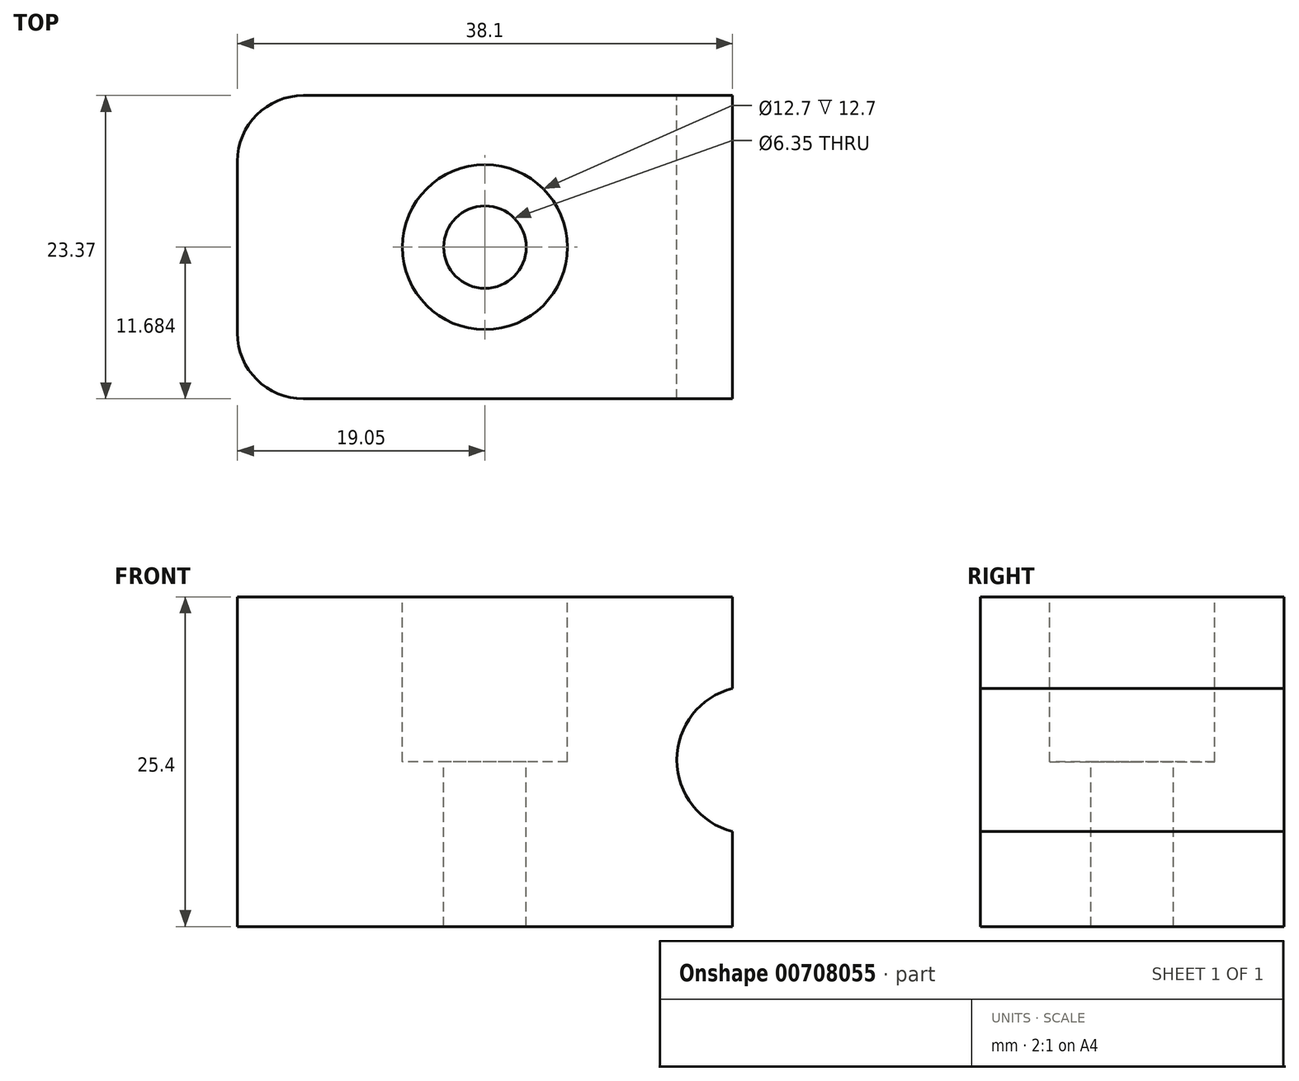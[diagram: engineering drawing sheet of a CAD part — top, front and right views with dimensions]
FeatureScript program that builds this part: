
annotation { "Feature Type Name" : "Feature", "Feature Type Description" : "" }
export const myFeature = defineFeature(function(context is Context, id is Id, definition is map)
    precondition{}
    {
        {
            var Q0;
            Q0=qCreatedBy(makeId("Top.planeOp"),FACE);
            var sketch = newSketch(context, id + "F0", { "sketchPlane" : qUnion([Q0])});
            skLineSegment(sketch, "E0.bottom", {"start": v(0, 0) * mm, "end": v(38.1, 0) * mm});
            skLineSegment(sketch, "E0.top", {"start": v(0, 23.37) * mm, "end": v(38.1, 23.37) * mm});
            skLineSegment(sketch, "E0.left", {"start": v(0, 0) * mm, "end": v(0, 23.37) * mm});
            skLineSegment(sketch, "E0.right", {"start": v(38.1, 0) * mm, "end": v(38.1, 23.37) * mm});
            skSolve(sketch);
        }
        {
            var Q0;
            Q0 = qSketchRegion(id + "F0", true);
            extrude(context, id + "F1", {"entities" : qUnion([Q0]), "depth" : 25.4 * mm, "offsetDistance" : 25.4 * mm});
        }
        {
            var Q0;
            Q0=makeQuery(id+"F1.opExtrude","CAP_FACE",FACE,{"disambiguationData":[OSD([sQuery(id+"F0.wireOp",EDGE,"E0.bottom"),sQuery(id+"F0.wireOp",EDGE,"E0.top"),sQuery(id+"F0.wireOp",EDGE,"E0.left"),sQuery(id+"F0.wireOp",EDGE,"E0.right")])],"isStart":false});
            var sketch = newSketch(context, id + "F2", { "sketchPlane" : qUnion([Q0])});
            skLineSegment(sketch, "E1", {"start": v(0, 23.37) * mm, "end": v(38.1, 0) * mm, "construction": true});
            skLineSegment(sketch, "E2", {"start": v(0, 0) * mm, "end": v(38.1, 23.37) * mm, "construction": true});
            skCircle(sketch, "E3", {"center": v(19.05, 11.68) * mm, "radius": 6.35 * mm});
            skSolve(sketch);
        }
        {
            var Q0;
            Q0=makeQuery(id+"F2.imprint","IMPRINT",FACE,{"disambiguationData":[TD([[makeQuery(id+"F2.imprint","IMPRINT",EDGE,{"derivedFrom":sQuery(id+"F2.wireOp",EDGE,"E3")}),1.0]])]});
            extrude(context, id + "F3", {"entities" : qUnion([Q0]), "operationType" : NewBodyOperationType.REMOVE, "oppositeDirection" : true, "depth" : 12.7 * mm, "offsetDistance" : 25.4 * mm});
        }
        {
            var Q0;
            Q0=makeQuery(id+"F3.boolean.opBoolean","COPY",FACE,{"derivedFrom":makeQuery(id+"F3.opExtrude","CAP_FACE",FACE,{"disambiguationData":[OSD([sQuery(id+"F2.wireOp",EDGE,"E3")])],"isStart":false})});
            var sketch = newSketch(context, id + "F4", { "sketchPlane" : qUnion([Q0])});
            skCircle(sketch, "E4", {"center": v(19.05, 11.68) * mm, "radius": 3.18 * mm});
            skSolve(sketch);
        }
        {
            var Q0;
            Q0=makeQuery(id+"F4.imprint","IMPRINT",FACE,{"disambiguationData":[TD([[makeQuery(id+"F4.imprint","IMPRINT",EDGE,{"derivedFrom":sQuery(id+"F4.wireOp",EDGE,"E4")}),1.0]])]});
            extrude(context, id + "F5", {"entities" : qUnion([Q0]), "operationType" : NewBodyOperationType.REMOVE, "oppositeDirection" : true, "depth" : 25.4 * mm, "offsetDistance" : 25.4 * mm});
        }
        {
            var Q0;
            Q0=makeQuery(id+"F1.opExtrude","SWEPT_EDGE",EDGE,{"disambiguationData":[OSD([sQuery(id+"F0.wireOp",EDGE,"E0.top"),sQuery(id+"F0.wireOp",EDGE,"E0.left")])]});
            var Q1;
            Q1=makeQuery(id+"F1.opExtrude","SWEPT_EDGE",EDGE,{"disambiguationData":[OSD([sQuery(id+"F0.wireOp",EDGE,"E0.bottom"),sQuery(id+"F0.wireOp",EDGE,"E0.left")])]});
            fillet(context, id + "F6", {"entities" : qUnion([Q0, Q1]), "radius" : 5.08 * mm, "tangentPropagation" : true, "allowEdgeOverflow" : false});
        }
        {
            var Q0;
            Q0=makeQuery(id+"F1.opExtrude","SWEPT_FACE",FACE,{"disambiguationData":[OSD([sQuery(id+"F0.wireOp",EDGE,"E0.top")])]});
            var sketch = newSketch(context, id + "F7", { "sketchPlane" : qUnion([Q0])});
            skArc(sketch, "E5", {"start": v(-38.1, 7.32) * mm, "mid": v(-33.82, 12.83) * mm, "end": v(-38.1, 18.35) * mm});
            skLineSegment(sketch, "E6", {"start": v(-38.1, 7.32) * mm, "end": v(-38.1, 18.35) * mm});
            skSolve(sketch);
        }
        {
            var Q0;
            Q0=makeQuery(id+"F7.imprint","IMPRINT",FACE,{"disambiguationData":[TD([[makeQuery(id+"F7.imprint","IMPRINT",EDGE,{"derivedFrom":sQuery(id+"F7.wireOp",EDGE,"E5")}),1.0]])]});
            extrude(context, id + "F8", {"entities" : qUnion([Q0]), "operationType" : NewBodyOperationType.REMOVE, "oppositeDirection" : true, "depth" : 25.4 * mm, "offsetDistance" : 25.4 * mm});
        }
    });
